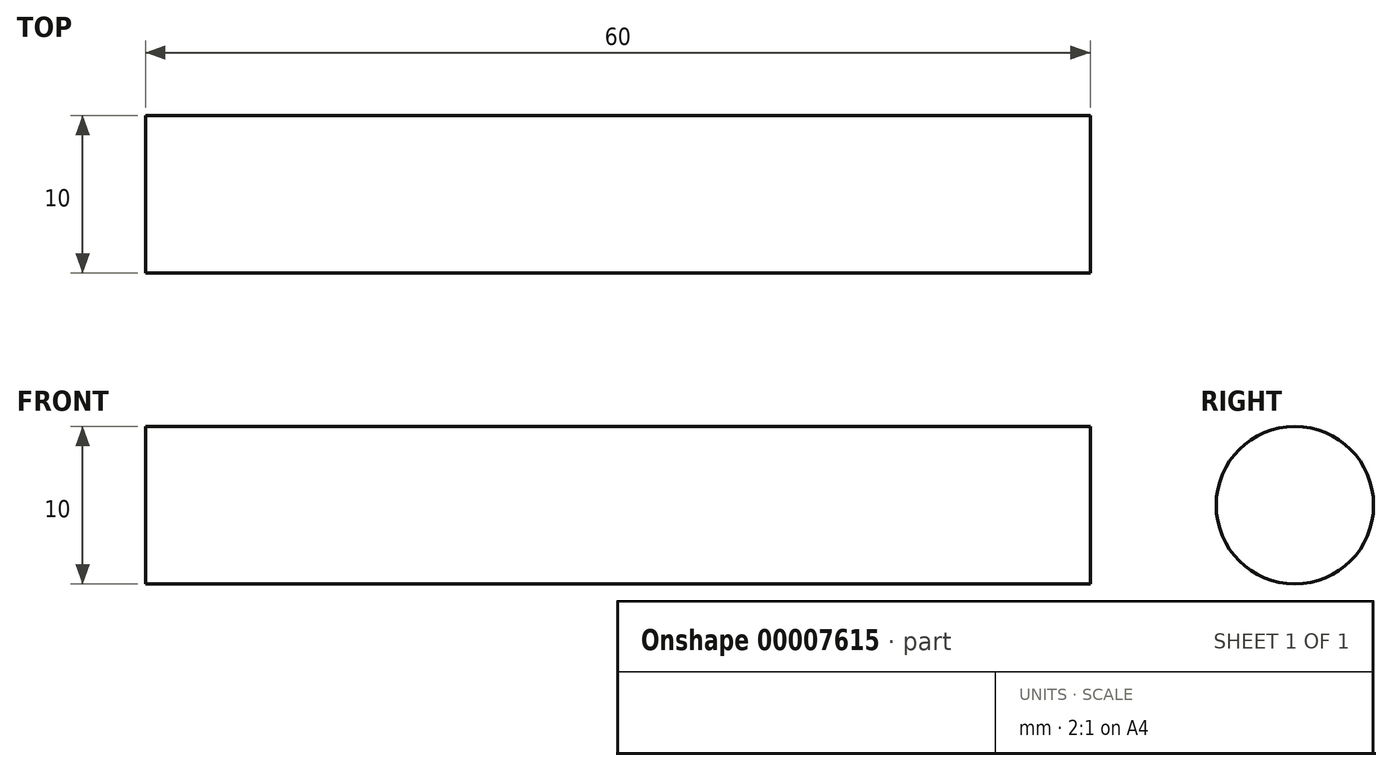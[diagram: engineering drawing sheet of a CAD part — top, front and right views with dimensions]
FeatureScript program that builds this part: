
annotation { "Feature Type Name" : "Feature", "Feature Type Description" : "" }
export const myFeature = defineFeature(function(context is Context, id is Id, definition is map)
    precondition{}
    {
        {
            var Q0;
            Q0=qCreatedBy(makeId("Right.planeOp"),FACE);
            var sketch = newSketch(context, id + "F0", { "sketchPlane" : qUnion([Q0])});
            skCircle(sketch, "E0", {"center": v(0, 0) * mm, "radius": 5 * mm});
            skSolve(sketch);
        }
        {
            var Q0;
            Q0 = qSketchRegion(id + "F0", true);
            extrude(context, id + "F1", {"entities" : qUnion([Q0]), "endBound" : BoundingType.SYMMETRIC, "depth" : 60 * mm});
        }
    });
